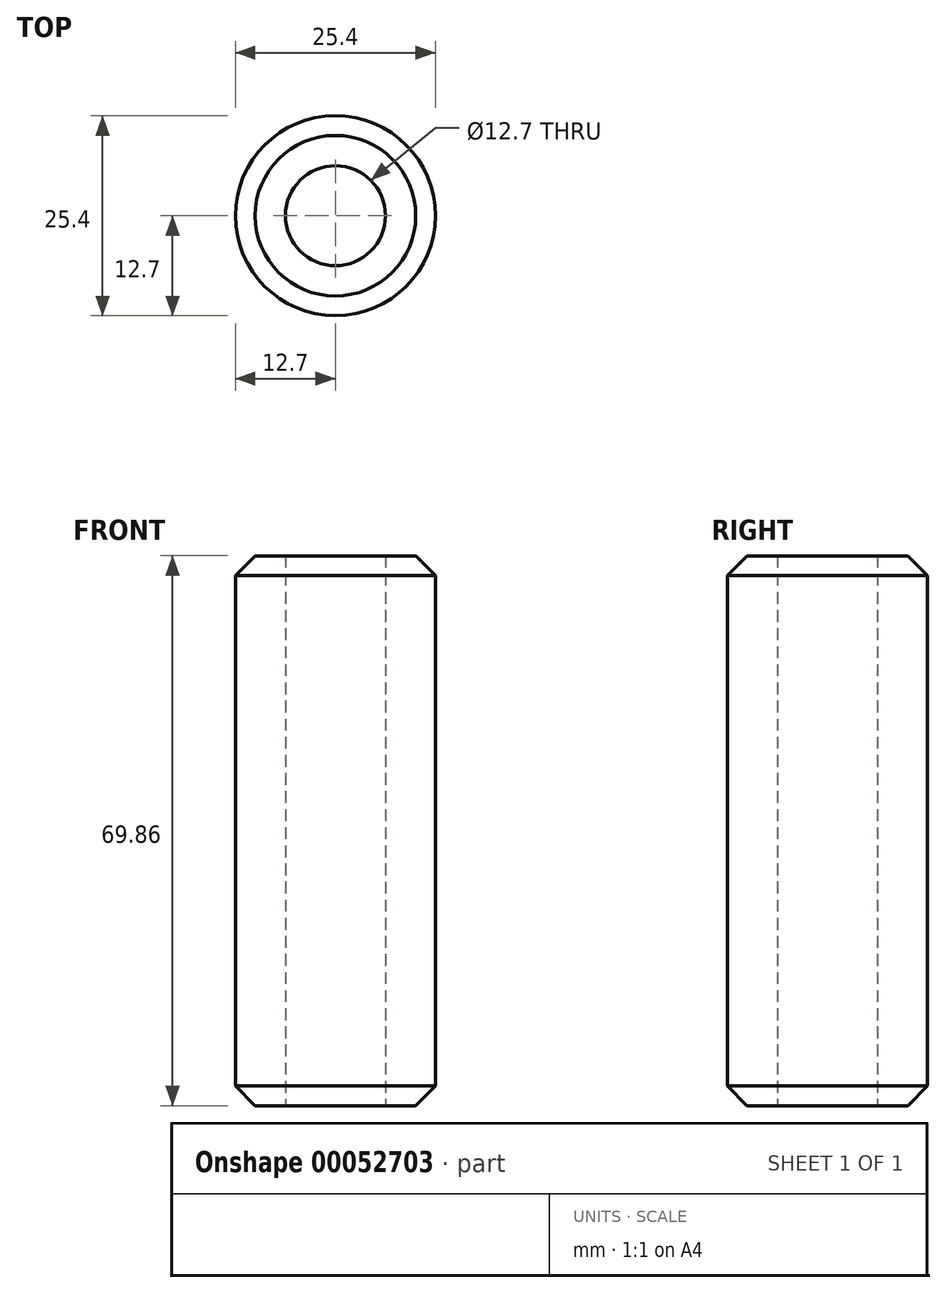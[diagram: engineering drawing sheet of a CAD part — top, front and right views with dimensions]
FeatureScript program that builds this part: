
annotation { "Feature Type Name" : "Feature", "Feature Type Description" : "" }
export const myFeature = defineFeature(function(context is Context, id is Id, definition is map)
    precondition{}
    {
        {
            var Q0;
            Q0=qCreatedBy(makeId("Top.planeOp"),FACE);
            var sketch = newSketch(context, id + "F0", { "sketchPlane" : qUnion([Q0])});
            skCircle(sketch, "E0", {"center": v(0, 0) * mm, "radius": 12.7 * mm});
            skCircle(sketch, "E1", {"center": v(0, 0) * mm, "radius": 6.35 * mm});
            skSolve(sketch);
        }
        {
            var Q0;
            Q0=makeQuery(id+"F0.imprint","IMPRINT",FACE,{"disambiguationData":[TD([[makeQuery(id+"F0.imprint","IMPRINT",EDGE,{"derivedFrom":sQuery(id+"F0.wireOp",EDGE,"E0")}),1.0]])]});
            extrude(context, id + "F1", {"entities" : qUnion([Q0]), "depth" : 69.85 * mm, "symmetric" : true});
        }
        {
            var Q0;
            Q0=makeQuery(id+"F1.opExtrude","CAP_EDGE",EDGE,{"disambiguationData":[OSD([sQuery(id+"F0.wireOp",EDGE,"E0")])],"isStart":false});
            var Q1;
            Q1=makeQuery(id+"F1.opExtrude","CAP_EDGE",EDGE,{"disambiguationData":[OSD([sQuery(id+"F0.wireOp",EDGE,"E0")])],"isStart":true});
            chamfer(context, id + "F2", {"entities" : qUnion([Q0, Q1]), "width" : 2.5 * mm, "tangentPropagation" : true});
        }
    });
